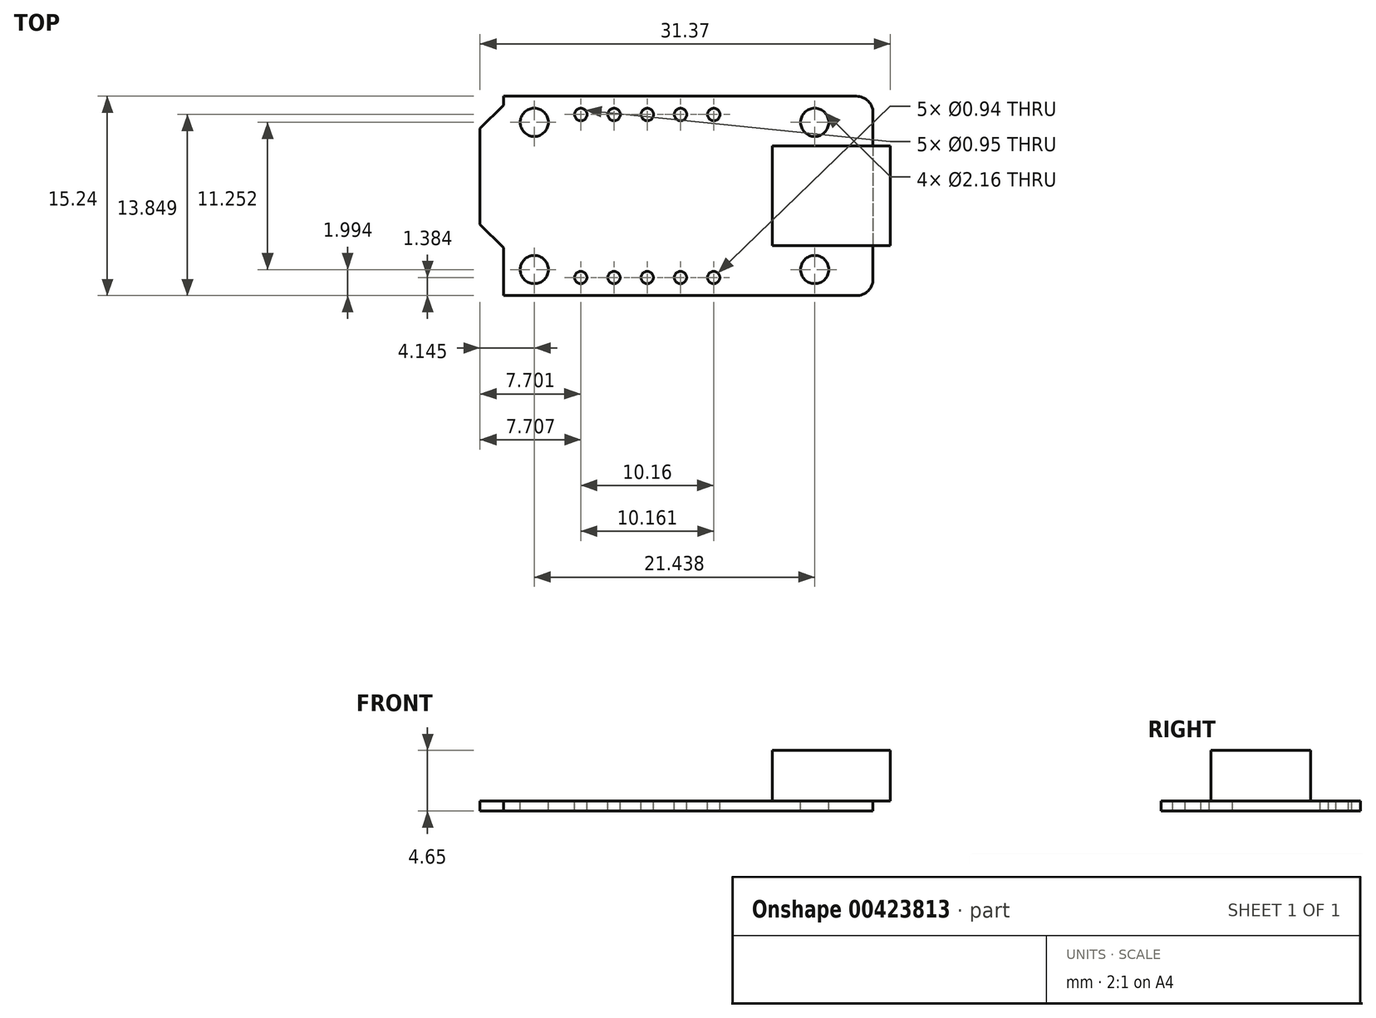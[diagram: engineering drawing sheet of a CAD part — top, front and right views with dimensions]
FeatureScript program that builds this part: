
annotation { "Feature Type Name" : "Feature", "Feature Type Description" : "" }
export const myFeature = defineFeature(function(context is Context, id is Id, definition is map)
    precondition{}
    {
        {
            var Q0;
            Q0=qCreatedBy(makeId("Top.planeOp"),FACE);
            var sketch = newSketch(context, id + "F0", { "sketchPlane" : qUnion([Q0])});
            skLineSegment(sketch, "E0.bottom", {"start": v(-1.27, 0) * mm, "end": v(-28.24, 0) * mm});
            skLineSegment(sketch, "E0.top", {"start": v(-1.27, -15.24) * mm, "end": v(-28.24, -15.24) * mm});
            skLineSegment(sketch, "E0.left", {"start": v(0, -1.27) * mm, "end": v(0, -13.97) * mm});
            skLineSegment(sketch, "E0.right", {"start": v(-28.24, 0) * mm, "end": v(-28.24, -0.68) * mm});
            skLineSegment(sketch, "E1", {"start": v(-28.24, -0.68) * mm, "end": v(-30.04, -2.47) * mm});
            skLineSegment(sketch, "E2", {"start": v(-30.04, -2.47) * mm, "end": v(-30.04, -9.79) * mm});
            skLineSegment(sketch, "E3", {"start": v(-30.04, -9.79) * mm, "end": v(-28.24, -11.58) * mm});
            skLineSegment(sketch, "E4.trimOffspring", {"start": v(-28.24, -11.58) * mm, "end": v(-28.24, -15.24) * mm});
            skPoint(sketch, "E5.visualSharp", {"position": v(0, 0) * mm});
            skArc(sketch, "E5.filletArc", {"start": v(0, -1.27) * mm, "mid": v(-0.37, -0.37) * mm, "end": v(-1.27, 0) * mm});
            skPoint(sketch, "E6.visualSharp", {"position": v(0, -15.24) * mm});
            skArc(sketch, "E6.filletArc", {"start": v(-1.27, -15.24) * mm, "mid": v(-0.37, -14.87) * mm, "end": v(0, -13.97) * mm});
            skSolve(sketch);
        }
        {
            var Q0;
            Q0=qSketchRegion(id+"F0",true);
            var Q1;
            Q1=qSketchRegion(id+"F2",true);
            extrude(context, id + "F1", {"entities" : qUnion([Q0, Q1]), "depth" : 0.79 * mm});
        }
        {
            var Q0;
            Q0=makeQuery(id+"F1.opExtrude","CAP_FACE",FACE,{"disambiguationData":[OSD([sQuery(id+"F0.wireOp",EDGE,"E0.bottom"),sQuery(id+"F0.wireOp",EDGE,"E0.top"),sQuery(id+"F0.wireOp",EDGE,"E0.left"),sQuery(id+"F0.wireOp",EDGE,"E0.right"),sQuery(id+"F0.wireOp",EDGE,"E1"),sQuery(id+"F0.wireOp",EDGE,"E2"),sQuery(id+"F0.wireOp",EDGE,"E3"),sQuery(id+"F0.wireOp",EDGE,"E4.trimOffspring"),sQuery(id+"F0.wireOp",EDGE,"E5.filletArc"),sQuery(id+"F0.wireOp",EDGE,"E6.filletArc")])],"isStart":false});
            var sketch = newSketch(context, id + "F2", { "sketchPlane" : qUnion([Q0])});
            skCircle(sketch, "E7", {"center": v(-25.9, -13.25) * mm, "radius": 1.08 * mm});
            skCircle(sketch, "E8", {"center": v(-25.9, -2) * mm, "radius": 1.08 * mm});
            skCircle(sketch, "E9", {"center": v(-4.46, -2) * mm, "radius": 1.08 * mm});
            skCircle(sketch, "E10", {"center": v(-4.46, -13.25) * mm, "radius": 1.08 * mm});
            skCircle(sketch, "E11", {"center": v(-22.33, -1.4) * mm, "radius": 0.48 * mm});
            skCircle(sketch, "E12.1.0.0", {"center": v(-19.8, -1.4) * mm, "radius": 0.48 * mm});
            skCircle(sketch, "E12.2.0.0", {"center": v(-17.25, -1.4) * mm, "radius": 0.48 * mm});
            skCircle(sketch, "E12.3.0.0", {"center": v(-14.71, -1.4) * mm, "radius": 0.48 * mm});
            skCircle(sketch, "E12.4.0.0", {"center": v(-12.17, -1.4) * mm, "radius": 0.48 * mm});
            skLineSegment(sketch, "E12.direction1", {"start": v(-22.33, -1.4) * mm, "end": v(-19.8, -1.4) * mm, "construction": true});
            skCircle(sketch, "E13", {"center": v(-22.34, -13.86) * mm, "radius": 0.47 * mm});
            skCircle(sketch, "E14.1.0.0", {"center": v(-19.8, -13.86) * mm, "radius": 0.47 * mm});
            skCircle(sketch, "E14.2.0.0", {"center": v(-17.26, -13.86) * mm, "radius": 0.47 * mm});
            skCircle(sketch, "E14.3.0.0", {"center": v(-14.72, -13.86) * mm, "radius": 0.47 * mm});
            skCircle(sketch, "E14.4.0.0", {"center": v(-12.18, -13.86) * mm, "radius": 0.47 * mm});
            skLineSegment(sketch, "E14.direction1", {"start": v(-22.34, -13.86) * mm, "end": v(-19.8, -13.86) * mm, "construction": true});
            skSolve(sketch);
        }
        {
            var Q0;
            Q0=qSketchRegion(id+"F2",true);
            extrude(context, id + "F3", {"entities" : qUnion([Q0]), "operationType" : NewBodyOperationType.REMOVE, "endBound" : BoundingType.THROUGH_ALL, "oppositeDirection" : true, "depth" : 25.4 * mm});
        }
        {
            var Q0;
            Q0=makeQuery(id+"F1.opExtrude","CAP_FACE",FACE,{"disambiguationData":[OSD([sQuery(id+"F0.wireOp",EDGE,"E0.bottom"),sQuery(id+"F0.wireOp",EDGE,"E0.top"),sQuery(id+"F0.wireOp",EDGE,"E0.left"),sQuery(id+"F0.wireOp",EDGE,"E0.right"),sQuery(id+"F0.wireOp",EDGE,"E1"),sQuery(id+"F0.wireOp",EDGE,"E2"),sQuery(id+"F0.wireOp",EDGE,"E3"),sQuery(id+"F0.wireOp",EDGE,"E4.trimOffspring"),sQuery(id+"F0.wireOp",EDGE,"E5.filletArc"),sQuery(id+"F0.wireOp",EDGE,"E6.filletArc")])],"isStart":false});
            var sketch = newSketch(context, id + "F4", { "sketchPlane" : qUnion([Q0])});
            skLineSegment(sketch, "E15.bottom", {"start": v(1.33, -3.81) * mm, "end": v(-7.7, -3.81) * mm});
            skLineSegment(sketch, "E15.top", {"start": v(1.33, -11.43) * mm, "end": v(-7.7, -11.43) * mm});
            skLineSegment(sketch, "E15.left", {"start": v(1.33, -3.8) * mm, "end": v(1.33, -11.43) * mm});
            skLineSegment(sketch, "E15.right", {"start": v(-7.7, -3.81) * mm, "end": v(-7.7, -11.43) * mm});
            skPoint(sketch, "E16", {"position": v(0, -7.62) * mm});
            skLineSegment(sketch, "E17", {"start": v(0, -7.62) * mm, "end": v(-17.46, -7.62) * mm, "construction": true});
            skPoint(sketch, "E18", {"position": v(-7.7, -7.62) * mm});
            skSolve(sketch);
        }
        {
            var Q0;
            Q0=qSketchRegion(id+"F4",true);
            extrude(context, id + "F5", {"entities" : qUnion([Q0]), "operationType" : NewBodyOperationType.ADD, "depth" : 3.86 * mm});
        }
    });
